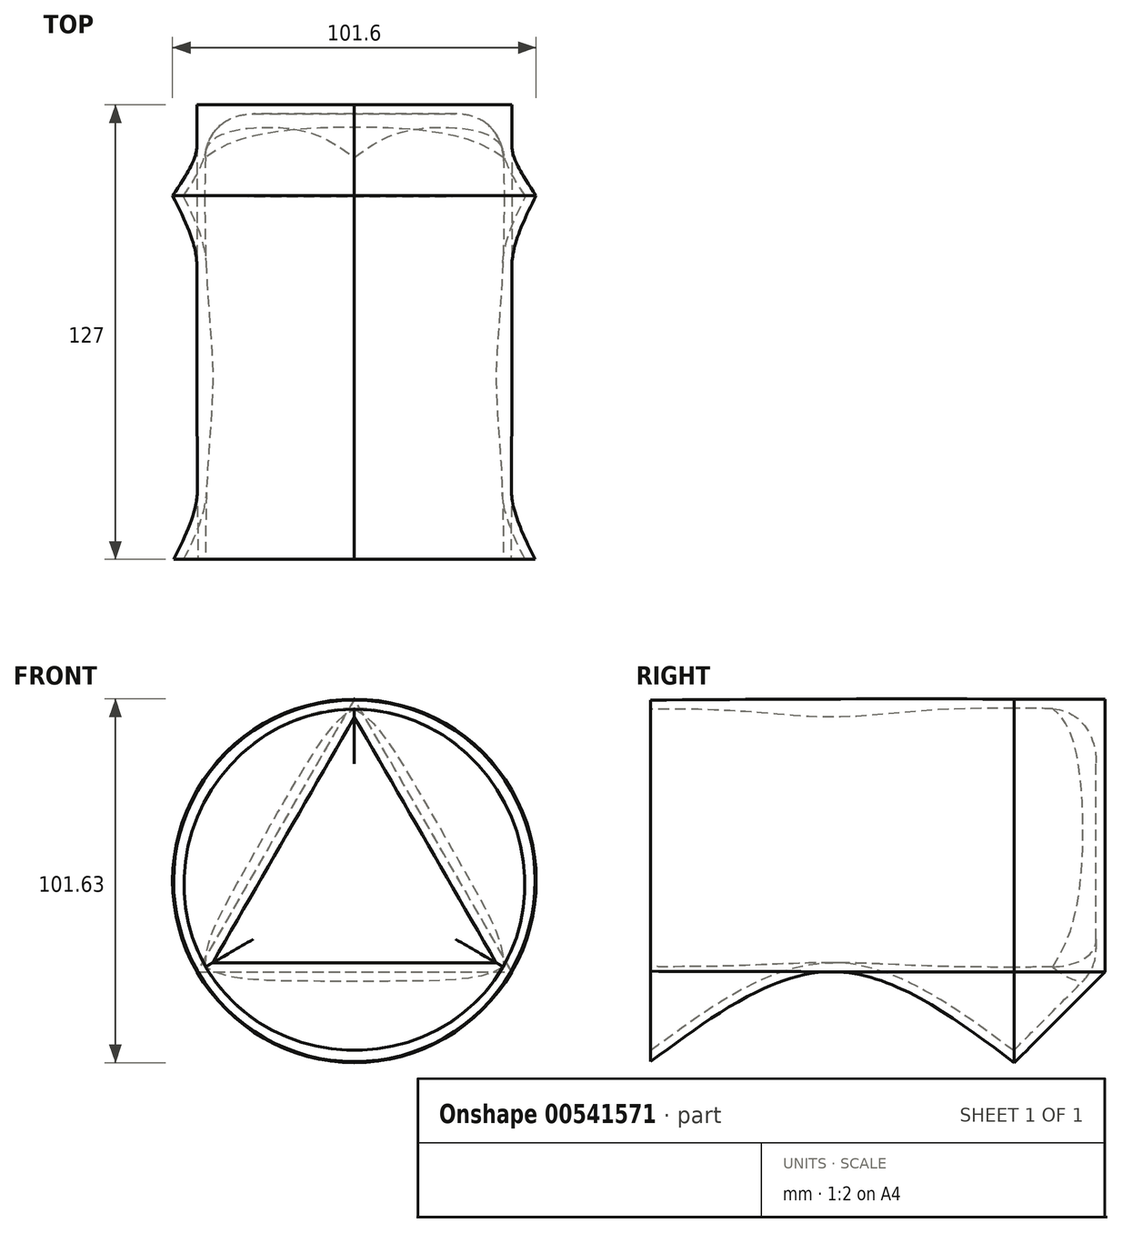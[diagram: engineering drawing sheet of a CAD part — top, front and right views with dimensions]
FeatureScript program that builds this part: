
annotation { "Feature Type Name" : "Feature", "Feature Type Description" : "" }
export const myFeature = defineFeature(function(context is Context, id is Id, definition is map)
    precondition{}
    {
        {
            var Q0;
            Q0=qCreatedBy(makeId("Front.planeOp"),FACE);
            var sketch = newSketch(context, id + "F0", { "sketchPlane" : qUnion([Q0])});
            skCircle(sketch, "E0", {"center": v(0, 0) * mm, "radius": 50.8 * mm});
            skSolve(sketch);
        }
        {
            var Q0;
            Q0=qCreatedBy(makeId("Front.planeOp"),FACE);
            cPlane(context, id + "F1", {"entities" : qUnion([Q0]), "cplaneType" : CPlaneType.OFFSET, "offset" : 50.8 * mm, "width" : 152.4 * mm, "height" : 152.4 * mm});
        }
        {
            var Q0;
            Q0=qCreatedBy(id+"F1.planeOp",FACE);
            var sketch = newSketch(context, id + "F2", { "sketchPlane" : qUnion([Q0])});
            skCircle(sketch, "E1.cCircle", {"center": v(0, 0) * mm, "radius": 25.4 * mm, "construction": true});
            skLineSegment(sketch, "E1.0", {"start": v(44, -25.4) * mm, "end": v(-44, -25.4) * mm});
            skLineSegment(sketch, "E1.1", {"start": v(-44, -25.4) * mm, "end": v(0, 50.8) * mm});
            skLineSegment(sketch, "E1.2", {"start": v(0, 50.8) * mm, "end": v(44, -25.4) * mm});
            skPoint(sketch, "E1.0.midPoint", {"position": v(0, -25.4) * mm});
            skSolve(sketch);
        }
        {
            var Q0;
            Q0=qCreatedBy(id+"F1.planeOp",FACE);
            cPlane(context, id + "F3", {"entities" : qUnion([Q0]), "cplaneType" : CPlaneType.OFFSET, "offset" : 50.8 * mm, "width" : 152.4 * mm, "height" : 152.4 * mm});
        }
        {
            var Q0;
            Q0=qCreatedBy(id+"F3.planeOp",FACE);
            var sketch = newSketch(context, id + "F4", { "sketchPlane" : qUnion([Q0])});
            skCircle(sketch, "E2", {"center": v(0, 0) * mm, "radius": 50.51 * mm});
            skSolve(sketch);
        }
        {
            var Q0;
            Q0=makeQuery(id+"F0.imprint","IMPRINT",FACE,{"disambiguationData":[TD([[makeQuery(id+"F0.imprint","IMPRINT",EDGE,{"derivedFrom":sQuery(id+"F0.wireOp",EDGE,"E0")}),1.0]])]});
            var Q1;
            Q1=makeQuery(id+"F2.imprint","IMPRINT",FACE,{"disambiguationData":[TD([[makeQuery(id+"F2.imprint","IMPRINT",EDGE,{"derivedFrom":sQuery(id+"F2.wireOp",EDGE,"E1.0")}),-1.0]])]});
            var Q2;
            Q2=makeQuery(id+"F4.imprint","IMPRINT",FACE,{"disambiguationData":[TD([[makeQuery(id+"F4.imprint","IMPRINT",EDGE,{"derivedFrom":sQuery(id+"F4.wireOp",EDGE,"E2")}),1.0]])]});
            loft(context, id + "F5", {"sheetProfilesArray" : [{ "sheetProfileEntities" : qUnion([Q0]) }, { "sheetProfileEntities" : qUnion([Q1]) }, { "sheetProfileEntities" : qUnion([Q2]) }]});
        }
        {
            var Q0;
            Q0=makeQuery(id+"F5.opLoft","CAP_FACE",FACE,{"disambiguationData":[OSD([makeQuery(id+"F0.imprint","IMPRINT",FACE,{"disambiguationData":[TD([[makeQuery(id+"F0.imprint","IMPRINT",EDGE,{"derivedFrom":sQuery(id+"F0.wireOp",EDGE,"E0")}),1.0]])]})])],"isStart":true});
            cPlane(context, id + "F6", {"entities" : qUnion([Q0]), "cplaneType" : CPlaneType.OFFSET, "offset" : 25.4 * mm, "width" : 152.4 * mm, "height" : 152.4 * mm});
        }
        {
            var Q0;
            Q0=qCreatedBy(id+"F6.planeOp",FACE);
            var sketch = newSketch(context, id + "F7", { "sketchPlane" : qUnion([Q0])});
            skCircle(sketch, "E3.cCircle", {"center": v(0, 0) * mm, "radius": 25.4 * mm, "construction": true});
            skLineSegment(sketch, "E3.0", {"start": v(44, -25.4) * mm, "end": v(-44, -25.4) * mm});
            skLineSegment(sketch, "E3.1", {"start": v(-44, -25.4) * mm, "end": v(0, 50.8) * mm});
            skLineSegment(sketch, "E3.2", {"start": v(0, 50.8) * mm, "end": v(44, -25.4) * mm});
            skPoint(sketch, "E3.0.midPoint", {"position": v(0, -25.4) * mm});
            skSolve(sketch);
        }
        {
            var Q1;
            Q1=makeQuery(id+"F7.imprint","IMPRINT",FACE,{"disambiguationData":[TD([[makeQuery(id+"F7.imprint","IMPRINT",EDGE,{"derivedFrom":sQuery(id+"F7.wireOp",EDGE,"E3.0")}),-1.0]])]});
            var Q2;
            Q2=makeQuery(id+"F5.opLoft","CAP_FACE",FACE,{"disambiguationData":[OSD([makeQuery(id+"F0.imprint","IMPRINT",FACE,{"disambiguationData":[TD([[makeQuery(id+"F0.imprint","IMPRINT",EDGE,{"derivedFrom":sQuery(id+"F0.wireOp",EDGE,"E0")}),1.0]])]})])],"isStart":true});
            loft(context, id + "F8", {"operationType" : NewBodyOperationType.ADD, "sheetProfilesArray" : [{ "sheetProfileEntities" : qUnion([Q1]) }, { "sheetProfileEntities" : qUnion([Q2]) }]});
        }
        {
            var Q0;
            Q0=makeQuery(id+"F5.opLoft","CAP_FACE",FACE,{"disambiguationData":[OSD([makeQuery(id+"F4.imprint","IMPRINT",FACE,{"disambiguationData":[TD([[makeQuery(id+"F4.imprint","IMPRINT",EDGE,{"derivedFrom":sQuery(id+"F4.wireOp",EDGE,"E2")}),1.0]])]})])],"isStart":true});
            shell(context, id + "F9", {"entities" : qUnion([Q0]), "thickness" : 2.54 * mm});
        }
        {
            var Q0;
            Q0=makeQuery(id+"F9.opShell","OFFSET_FACE",FACE,{"disambiguationData":[OSD([makeQuery(id+"F7.imprint","IMPRINT",FACE,{"disambiguationData":[TD([[makeQuery(id+"F7.imprint","IMPRINT",EDGE,{"derivedFrom":sQuery(id+"F7.wireOp",EDGE,"E3.0")}),-1.0]])]})])]});
            fillet(context, id + "F10", {"entities" : qUnion([Q0]), "radius" : 12.7 * mm, "tangentPropagation" : true, "allowEdgeOverflow" : false});
        }
    });
